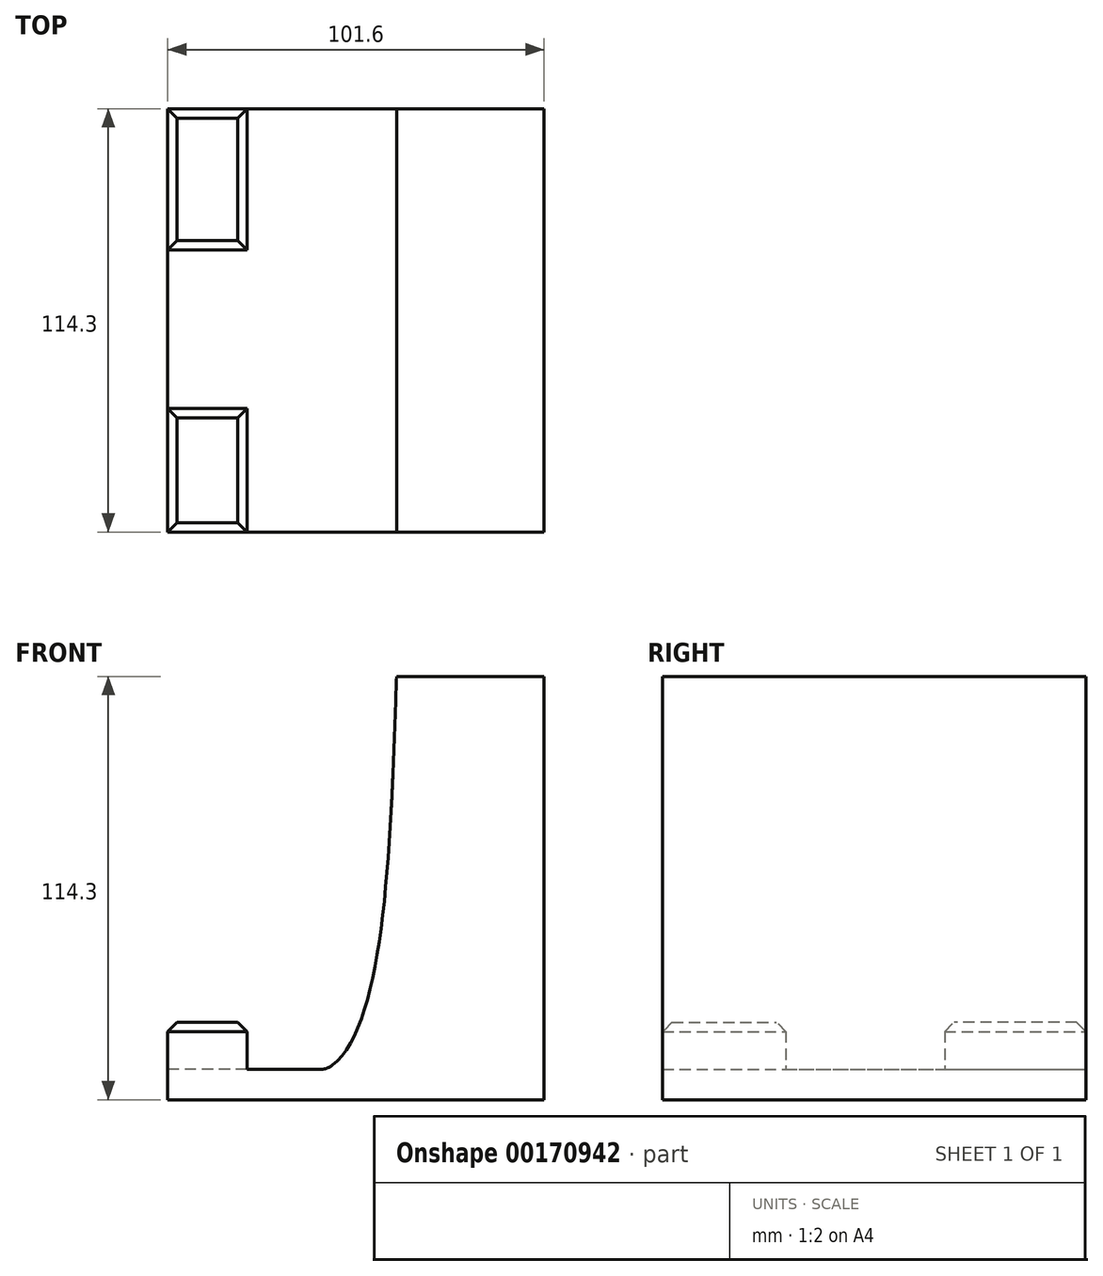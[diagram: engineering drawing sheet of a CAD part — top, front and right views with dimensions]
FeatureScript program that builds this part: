
annotation { "Feature Type Name" : "Feature", "Feature Type Description" : "" }
export const myFeature = defineFeature(function(context is Context, id is Id, definition is map)
    precondition{}
    {
        {
            var Q0;
            Q0=qCreatedBy(makeId("Front.planeOp"),FACE);
            var sketch = newSketch(context, id + "F6", { "sketchPlane" : qUnion([Q0])});
            skLineSegment(sketch, "E0", {"start": v(-11.8, 88.9) * mm, "end": v(28.03, 88.9) * mm});
            skLineSegment(sketch, "E1", {"start": v(28.03, 88.9) * mm, "end": v(28.03, -25.4) * mm});
            skLineSegment(sketch, "E2", {"start": v(28.03, -25.4) * mm, "end": v(-73.57, -25.4) * mm});
            skLineSegment(sketch, "E3", {"start": v(-73.57, -25.4) * mm, "end": v(-73.57, -17.17) * mm});
            skFitSpline(sketch, "E4", {"points": [v(-73.57, 0) * mm, v(-30.72, -17.17) * mm, v(-11.8, 88.9) * mm], "startDerivative": vector(123.55, -86.71) * mm, "endDerivative": vector(8.03, 241.65) * mm});
            skArc(sketch, "E5", {"start": v(-13.26, 52.54) * mm, "mid": v(-9.23, 57.93) * mm, "end": v(-12.72, 63.67) * mm});
            skLineSegment(sketch, "E6", {"start": v(-30.72, -17.17) * mm, "end": v(-49.79, -17.17) * mm});
            skPoint(sketch, "E7.visualSharp", {"position": v(-56.12, -17.17) * mm});
            skLineSegment(sketch, "E8", {"start": v(-49.79, -17.17) * mm, "end": v(-73.57, -17.17) * mm});
            skPoint(sketch, "E9.start.orphan", {"position": v(-56.14, 0) * mm});
            skSolve(sketch);
        }
        {
            var Q0;
            Q0 = qSketchRegion(id + "F6", true);
            var Q1;
            Q1=makeQuery(id+"F6.imprint","IMPRINT",FACE,{"disambiguationData":[TD([[makeQuery(id+"F6.imprint","IMPRINT",EDGE,{"derivedFrom":sQuery(id+"F6.wireOp",EDGE,"E0")}),-1.0]])]});
            extrude(context, id + "F7", {"entities" : qUnion([Q0, Q1]), "depth" : 114.3 * mm});
        }
        {
            var Q0;
            Q0=makeQuery(id+"F7.opExtrude","SWEPT_FACE",FACE,{"disambiguationData":[OSD([sQuery(id+"F6.wireOp",EDGE,"E6"),sQuery(id+"F6.wireOp",EDGE,"E8")])]});
            var sketch = newSketch(context, id + "F0", { "sketchPlane" : qUnion([Q0])});
            skLineSegment(sketch, "E10.bottom", {"start": v(-73.57, -114.3) * mm, "end": v(-52.14, -114.3) * mm});
            skLineSegment(sketch, "E10.top", {"start": v(-73.57, 0) * mm, "end": v(-52.14, 0) * mm});
            skLineSegment(sketch, "E10.left", {"start": v(-73.57, -114.3) * mm, "end": v(-73.57, -81) * mm});
            skLineSegment(sketch, "E10.right", {"start": v(-52.14, -114.3) * mm, "end": v(-52.14, 0) * mm});
            skLineSegment(sketch, "E11.bottom", {"start": v(-52.14, -81) * mm, "end": v(-73.57, -81) * mm});
            skLineSegment(sketch, "E11.top", {"start": v(-52.14, -38.15) * mm, "end": v(-73.57, -38.15) * mm});
            skLineSegment(sketch, "E11.right", {"start": v(-73.57, -81) * mm, "end": v(-73.57, -38.15) * mm});
            skLineSegment(sketch, "E12.trimOffspring", {"start": v(-73.57, -38.15) * mm, "end": v(-73.57, 0) * mm});
            skSolve(sketch);
        }
        {
            var Q0;
            {var subQ0=sQuery(id+"F0.wireOp",EDGE,"E10.bottom");Q0=makeQuery(id+"F0.imprint","IMPRINT",FACE,{"disambiguationData":[TD([[makeQuery(id+"F0.imprint","IMPRINT",EDGE,{"derivedFrom":subQ0}),-1.0]])]});}
            extrude(context, id + "F8", {"entities" : qUnion([Q0]), "operationType" : NewBodyOperationType.ADD, "depth" : 12.7 * mm});
        }
        {
            var Q0;
            {var subQ0=sQuery(id+"F0.wireOp",EDGE,"E10.top");Q0=makeQuery(id+"F0.imprint","IMPRINT",FACE,{"disambiguationData":[TD([[makeQuery(id+"F0.imprint","IMPRINT",EDGE,{"derivedFrom":subQ0}),1.0]])]});}
            extrude(context, id + "F9", {"entities" : qUnion([Q0]), "operationType" : NewBodyOperationType.ADD, "depth" : 12.7 * mm});
        }
        {
            var Q0;
            Q0=makeQuery(id+"F9.opExtrude","CAP_EDGE",EDGE,{"disambiguationData":[OSD([sQuery(id+"F0.wireOp",EDGE,"E10.top")])],"isStart":false});
            chamfer(context, id + "F10", {"entities" : qUnion([Q0]), "width" : 2.54 * mm, "tangentPropagation" : true});
        }
        {
            var Q0;
            Q0=makeQuery(id+"F9.opExtrude","CAP_EDGE",EDGE,{"disambiguationData":[OSD([sQuery(id+"F0.wireOp",EDGE,"E10.right")])],"isStart":false});
            chamfer(context, id + "F1", {"entities" : qUnion([Q0]), "width" : 2.54 * mm, "tangentPropagation" : true});
        }
        {
            var Q0;
            Q0=makeQuery(id+"F9.opExtrude","CAP_EDGE",EDGE,{"disambiguationData":[OSD([sQuery(id+"F0.wireOp",EDGE,"E12.trimOffspring")])],"isStart":false});
            chamfer(context, id + "F11", {"entities" : qUnion([Q0]), "width" : 2.54 * mm, "tangentPropagation" : true});
        }
        {
            var Q0;
            Q0=makeQuery(id+"F9.opExtrude","CAP_EDGE",EDGE,{"disambiguationData":[OSD([sQuery(id+"F0.wireOp",EDGE,"E11.top")])],"isStart":false});
            chamfer(context, id + "F2", {"entities" : qUnion([Q0]), "width" : 2.54 * mm, "tangentPropagation" : true});
        }
        {
            var Q0;
            Q0=makeQuery(id+"F8.opExtrude","CAP_EDGE",EDGE,{"disambiguationData":[OSD([sQuery(id+"F0.wireOp",EDGE,"E10.bottom")])],"isStart":false});
            chamfer(context, id + "F12", {"entities" : qUnion([Q0]), "width" : 2.54 * mm, "tangentPropagation" : true});
        }
        {
            var Q0;
            Q0=makeQuery(id+"F8.opExtrude","CAP_EDGE",EDGE,{"disambiguationData":[OSD([sQuery(id+"F0.wireOp",EDGE,"E10.left")])],"isStart":false});
            chamfer(context, id + "F3", {"entities" : qUnion([Q0]), "width" : 2.54 * mm, "tangentPropagation" : true});
        }
        {
            var Q0;
            Q0=makeQuery(id+"F8.opExtrude","CAP_EDGE",EDGE,{"disambiguationData":[OSD([sQuery(id+"F0.wireOp",EDGE,"E11.bottom")])],"isStart":false});
            chamfer(context, id + "F4", {"entities" : qUnion([Q0]), "width" : 2.54 * mm, "tangentPropagation" : true});
        }
        {
            var Q0;
            Q0=makeQuery(id+"F8.opExtrude","CAP_EDGE",EDGE,{"disambiguationData":[OSD([sQuery(id+"F0.wireOp",EDGE,"E10.right")])],"isStart":false});
            chamfer(context, id + "F5", {"entities" : qUnion([Q0]), "width" : 2.54 * mm, "tangentPropagation" : true});
        }
        {
            var Q0;
            Q0=makeQuery(id+"F7.opExtrude","SWEPT_EDGE",EDGE,{"disambiguationData":[OSD([sQuery(id+"F6.wireOp",EDGE,"E4"),sQuery(id+"F6.wireOp",EDGE,"E6")])]});
            fillet(context, id + "F13", {"entities" : qUnion([Q0]), "radius" : 5.08 * mm, "tangentPropagation" : true, "allowEdgeOverflow" : false});
        }
    });
